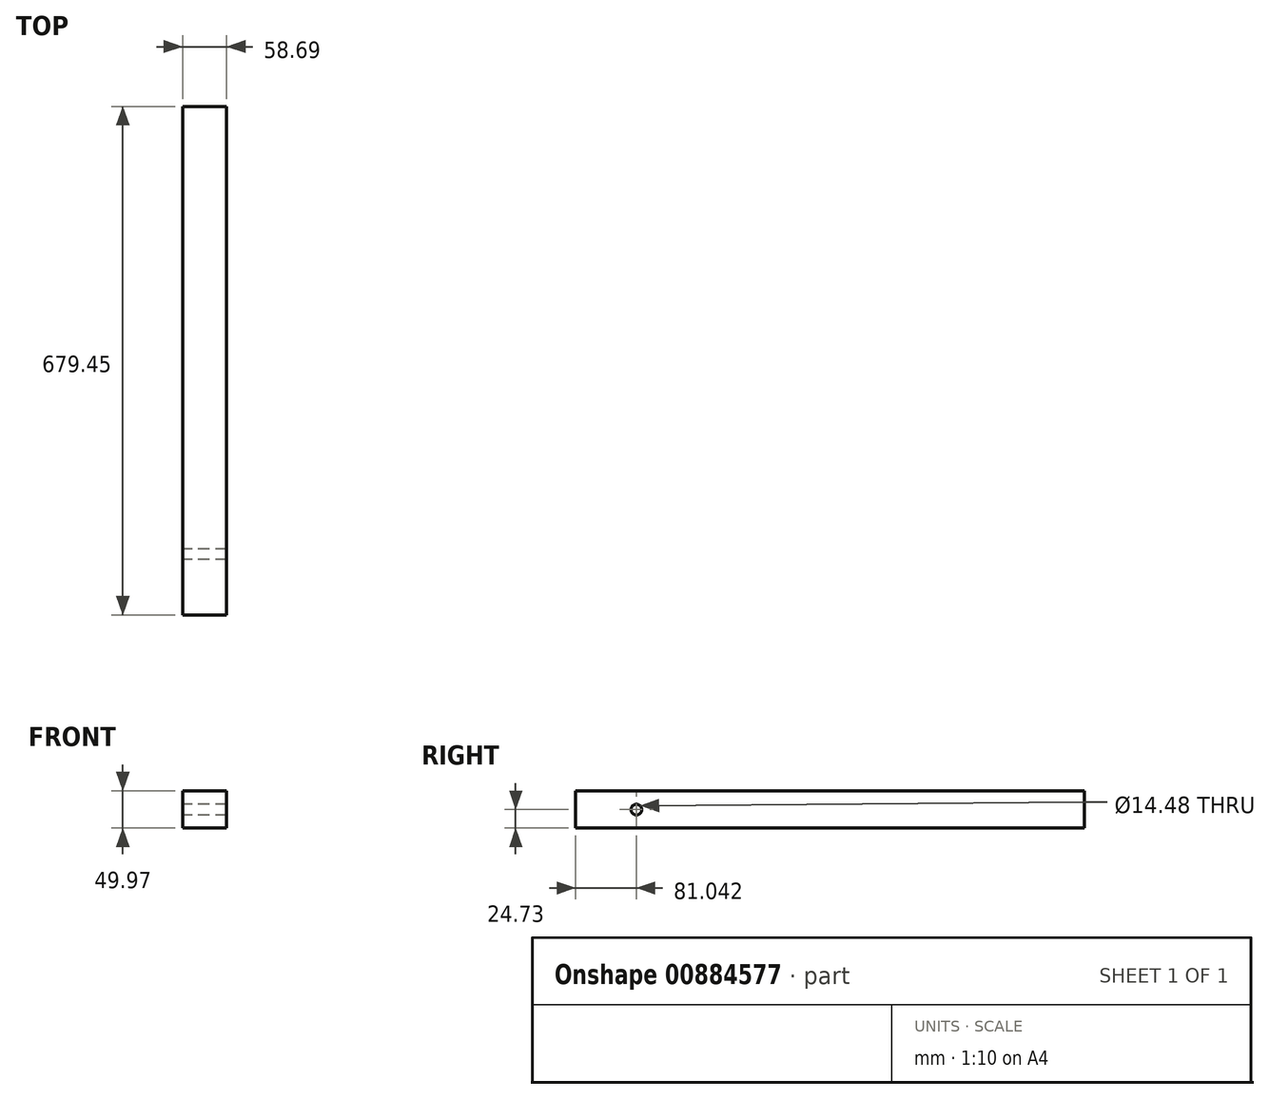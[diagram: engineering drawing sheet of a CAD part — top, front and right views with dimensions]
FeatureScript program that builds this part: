
annotation { "Feature Type Name" : "Feature", "Feature Type Description" : "" }
export const myFeature = defineFeature(function(context is Context, id is Id, definition is map)
    precondition{}
    {
        {
            var Q0;
            Q0=qCreatedBy(makeId("Front.planeOp"),FACE);
            var sketch = newSketch(context, id + "F0", { "sketchPlane" : qUnion([Q0])});
            skLineSegment(sketch, "E0.bottom", {"start": v(-30.47, 0) * mm, "end": v(28.22, 0) * mm});
            skLineSegment(sketch, "E0.top", {"start": v(-30.47, 49.97) * mm, "end": v(28.22, 49.97) * mm});
            skLineSegment(sketch, "E0.left", {"start": v(-30.47, 0) * mm, "end": v(-30.47, 49.97) * mm});
            skLineSegment(sketch, "E0.right", {"start": v(28.22, 0) * mm, "end": v(28.22, 49.97) * mm});
            skSolve(sketch);
        }
        {
            var Q0;
            Q0=makeQuery(id+"F0.imprint","IMPRINT",FACE,{"disambiguationData":[TD([[makeQuery(id+"F0.imprint","IMPRINT",EDGE,{"derivedFrom":sQuery(id+"F0.wireOp",EDGE,"E0.bottom")}),1.0]])]});
            var Q1;
            Q1 = qBodyType(qCreatedBy(id + "F0" ,EDGE), BodyType.WIRE);
            extrude(context, id + "F1", {"entities" : qUnion([Q0]), "surfaceOperationType" : NewSurfaceOperationType.ADD, "surfaceEntities" : qUnion([Q1]), "oppositeDirection" : true, "depth" : 711.2 * mm, "offsetDistance" : 25.4 * mm, "hasSecondDirection" : true, "secondDirectionOppositeDirection" : true, "secondDirectionDepth" : 31.75 * mm});
        }
        {
            var Q0;
            Q0=makeQuery(id+"F1.opExtrude","SWEPT_FACE",FACE,{"disambiguationData":[OSD([sQuery(id+"F0.wireOp",EDGE,"E0.left")])]});
            var sketch = newSketch(context, id + "F2", { "sketchPlane" : qUnion([Q0])});
            skCircle(sketch, "E1", {"center": v(86.45, 24.72) * mm, "radius": 6.6 * mm});
            skSolve(sketch);
        }
        {
            var Q0;
            {var subQ0=sQuery(id+"F0.wireOp",EDGE,"E0.left");Q0=makeQuery(id+"F2.imprint","IMPRINT",FACE,{"disambiguationData":[TD([[makeQuery(id+"F2.imprint","IMPRINT",EDGE,{"derivedFrom":makeQuery(id+"F1.opExtrude","CAP_EDGE",EDGE,{"disambiguationData":[OSD([subQ0])],"isStart":true})}),1.0]])]});}
            var sketch = newSketch(context, id + "F3", { "sketchPlane" : qUnion([Q0])});
            skCircle(sketch, "E2", {"center": v(-112.8, 24.73) * mm, "radius": 3.97 * mm});
            skSolve(sketch);
        }
        {
            var Q0;
            Q0=sQuery(id+"F3.wireOp",VERTEX,"E2.center");
            var Q1;
            Q1=makeQuery(id+"F1.opExtrude","SWEPT_BODY",BODY,{"disambiguationData":[OSD([sQuery(id+"F0.wireOp",EDGE,"E0.bottom"),sQuery(id+"F0.wireOp",EDGE,"E0.top"),sQuery(id+"F0.wireOp",EDGE,"E0.left"),sQuery(id+"F0.wireOp",EDGE,"E0.right")])]});
            hole(context, id + "F4", {"style" : HoleStyle.SIMPLE, "endStyle" : HoleEndStyle.THROUGH, "holeDiameter" : 14.48 * mm, "majorDiameter" : 6.35 * mm, "isTappedThrough" : true, "tappedDepth" : 12.7 * mm, "tapClearance" : 3, "locations" : qUnion([Q0]), "scope" : qUnion([Q1])});
        }
    });
